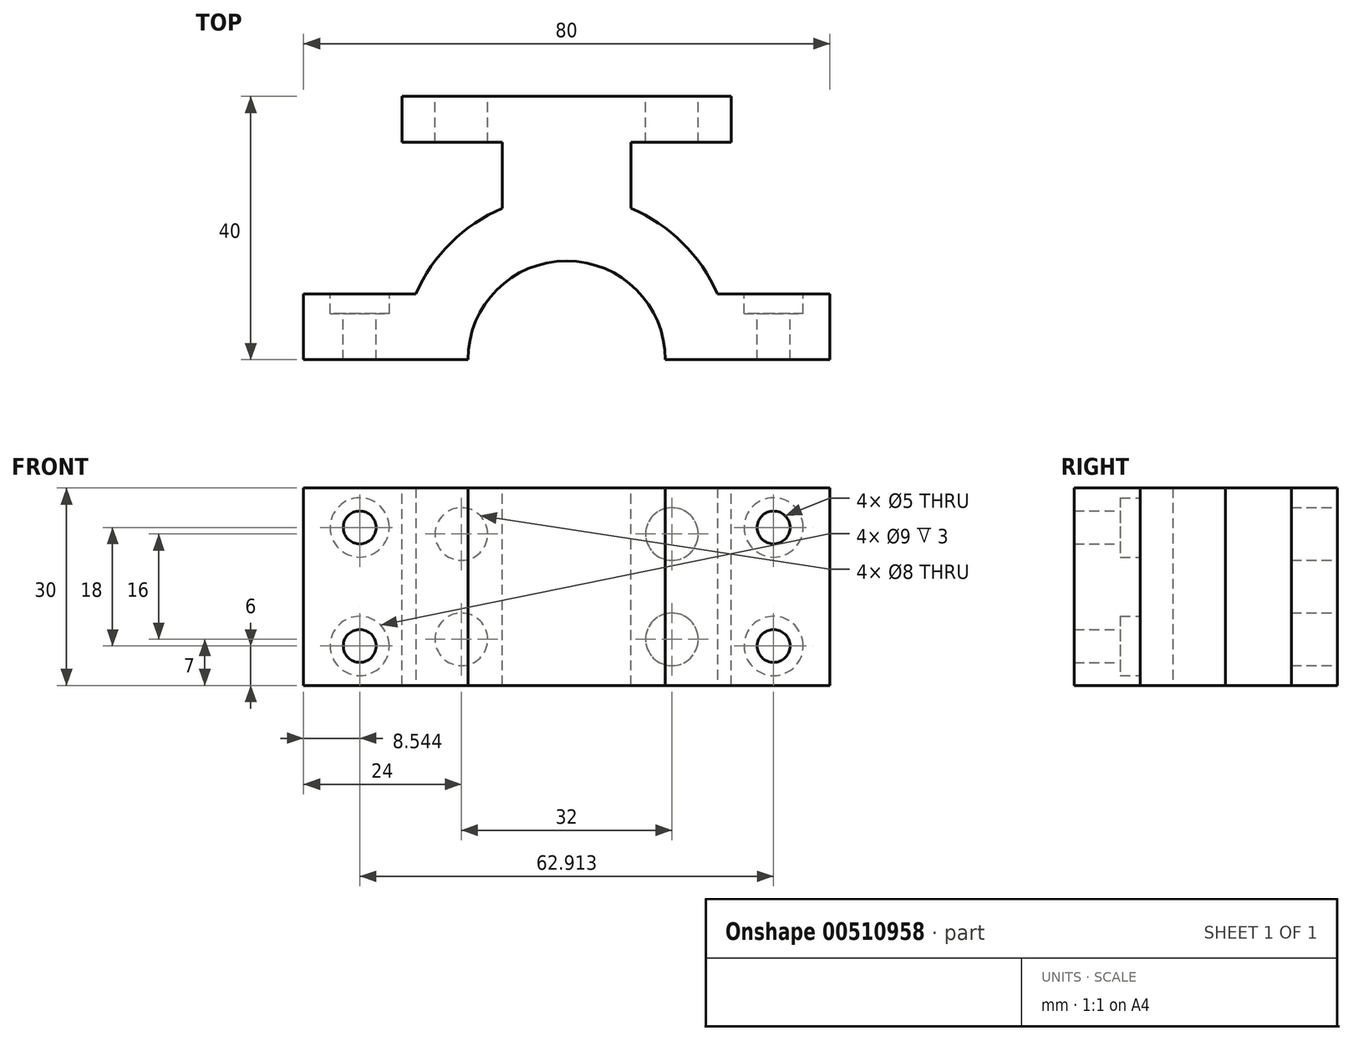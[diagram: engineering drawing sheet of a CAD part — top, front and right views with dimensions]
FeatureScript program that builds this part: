
annotation { "Feature Type Name" : "Feature", "Feature Type Description" : "" }
export const myFeature = defineFeature(function(context is Context, id is Id, definition is map)
    precondition{}
    {
        {
            var Q0;
            Q0=qCreatedBy(makeId("Top.planeOp"),FACE);
            var sketch = newSketch(context, id + "F0", { "sketchPlane" : qUnion([Q0])});
            skArc(sketch, "E0", {"start": v(15, 0) * mm, "mid": v(0, 15) * mm, "end": v(-15, 0) * mm});
            skArc(sketch, "E1.0", {"start": v(22.91, 10) * mm, "mid": v(0, 25) * mm, "end": v(-22.91, 10) * mm});
            skLineSegment(sketch, "E2", {"start": v(-22.91, 10) * mm, "end": v(-40, 10) * mm});
            skLineSegment(sketch, "E3", {"start": v(-40, 10) * mm, "end": v(-40, 0) * mm});
            skLineSegment(sketch, "E4", {"start": v(40, 0) * mm, "end": v(40, 10) * mm});
            skLineSegment(sketch, "E5", {"start": v(40, 10) * mm, "end": v(22.91, 10) * mm});
            skLineSegment(sketch, "E6", {"start": v(-40, 0) * mm, "end": v(-15, 0) * mm});
            skLineSegment(sketch, "E7", {"start": v(15, 0) * mm, "end": v(40, 0) * mm});
            skSolve(sketch);
        }
        {
            var Q0;
            Q0=qSketchRegion(id+"F0",true);
            extrude(context, id + "F1", {"entities" : qUnion([Q0]), "endBound" : BoundingType.SYMMETRIC, "depth" : 30 * mm});
        }
        {
            var Q0;
            Q0=makeQuery(id+"F1.opExtrude","SWEPT_FACE",FACE,{"disambiguationData":[OSD([sQuery(id+"F0.wireOp",EDGE,"E5")])]});
            var sketch = newSketch(context, id + "F2", { "sketchPlane" : qUnion([Q0])});
            skCircle(sketch, "E8", {"center": v(-31.46, 9) * mm, "radius": 2.5 * mm});
            skPoint(sketch, "E8.centerSnap0", {"position": v(-31.46, 15) * mm});
            skCircle(sketch, "E9.MirrorC", {"center": v(-31.46, -9) * mm, "radius": 2.5 * mm});
            skCircle(sketch, "E10.MirrorC", {"center": v(31.46, -9) * mm, "radius": 2.5 * mm});
            skCircle(sketch, "E11.MirrorC", {"center": v(31.46, 9) * mm, "radius": 2.5 * mm});
            skSolve(sketch);
        }
        {
            var Q0;
            Q0=qSketchRegion(id+"F2",true);
            extrude(context, id + "F3", {"entities" : qUnion([Q0]), "operationType" : NewBodyOperationType.REMOVE, "oppositeDirection" : true, "depth" : 15 * mm});
        }
        {
            var Q0;
            Q0=makeQuery(id+"F1.opExtrude","SWEPT_FACE",FACE,{"disambiguationData":[OSD([sQuery(id+"F0.wireOp",EDGE,"E2")])]});
            var sketch = newSketch(context, id + "F4", { "sketchPlane" : qUnion([Q0])});
            skCircle(sketch, "E12.0", {"center": v(31.46, 9) * mm, "radius": 2.5 * mm});
            skCircle(sketch, "E13.0", {"center": v(31.46, 9) * mm, "radius": 4.5 * mm});
            skCircle(sketch, "E14.MirrorC", {"center": v(31.46, -9) * mm, "radius": 4.5 * mm});
            skCircle(sketch, "E15.MirrorC", {"center": v(-31.46, -9) * mm, "radius": 4.5 * mm});
            skCircle(sketch, "E16.MirrorC", {"center": v(-31.46, 9) * mm, "radius": 4.5 * mm});
            skSolve(sketch);
        }
        {
            var Q0;
            Q0 = qSketchRegion(id + "F4", true);
            extrude(context, id + "F5", {"entities" : qUnion([Q0]), "operationType" : NewBodyOperationType.REMOVE, "oppositeDirection" : true, "depth" : 3 * mm});
        }
        {
            var Q0;
            Q0=makeQuery(id+"F1.opExtrude","CAP_FACE",FACE,{"disambiguationData":[OSD([sQuery(id+"F0.wireOp",EDGE,"E0"),sQuery(id+"F0.wireOp",EDGE,"E1.0"),sQuery(id+"F0.wireOp",EDGE,"E2"),sQuery(id+"F0.wireOp",EDGE,"E3"),sQuery(id+"F0.wireOp",EDGE,"E4"),sQuery(id+"F0.wireOp",EDGE,"E5"),sQuery(id+"F0.wireOp",EDGE,"E6"),sQuery(id+"F0.wireOp",EDGE,"E7")])],"isStart":false});
            var sketch = newSketch(context, id + "F6", { "sketchPlane" : qUnion([Q0])});
            skLineSegment(sketch, "E17.bottom", {"start": v(-9.8, 23) * mm, "end": v(9.8, 23) * mm});
            skLineSegment(sketch, "E17.top", {"start": v(-9.8, 33) * mm, "end": v(9.8, 33) * mm});
            skLineSegment(sketch, "E17.left", {"start": v(-9.8, 23) * mm, "end": v(-9.8, 33) * mm});
            skLineSegment(sketch, "E17.right", {"start": v(9.8, 23) * mm, "end": v(9.8, 33) * mm});
            skLineSegment(sketch, "E18.bottom", {"start": v(0, 33) * mm, "end": v(25, 33) * mm});
            skLineSegment(sketch, "E18.top", {"start": v(0, 40) * mm, "end": v(25, 40) * mm});
            skLineSegment(sketch, "E18.left", {"start": v(0, 33) * mm, "end": v(0, 40) * mm});
            skLineSegment(sketch, "E18.right", {"start": v(25, 33) * mm, "end": v(25, 40) * mm});
            skLineSegment(sketch, "E19.MirrorCS", {"start": v(0, 40) * mm, "end": v(-25, 40) * mm});
            skLineSegment(sketch, "E20.MirrorCS", {"start": v(-25, 33) * mm, "end": v(-25, 40) * mm});
            skLineSegment(sketch, "E21.MirrorCS", {"start": v(0, 33) * mm, "end": v(-25, 33) * mm});
            skSolve(sketch);
        }
        {
            var Q0;
            Q0 = qSketchRegion(id + "F6", true);
            extrude(context, id + "F7", {"entities" : qUnion([Q0]), "operationType" : NewBodyOperationType.ADD, "oppositeDirection" : true, "depth" : 30 * mm});
        }
        {
            var Q0;
            Q0=makeQuery(id+"F7.opExtrude","SWEPT_FACE",FACE,{"disambiguationData":[OSD([sQuery(id+"F6.wireOp",EDGE,"E18.top"),sQuery(id+"F6.wireOp",EDGE,"E19.MirrorCS")])]});
            var sketch = newSketch(context, id + "F8", { "sketchPlane" : qUnion([Q0])});
            skCircle(sketch, "E22", {"center": v(16, 8) * mm, "radius": 4 * mm});
            skCircle(sketch, "E23.MirrorC", {"center": v(16, -8) * mm, "radius": 4 * mm});
            skCircle(sketch, "E24.MirrorC", {"center": v(-16, -8) * mm, "radius": 4 * mm});
            skCircle(sketch, "E25.MirrorC", {"center": v(-16, 8) * mm, "radius": 4 * mm});
            skSolve(sketch);
        }
        {
            var Q0;
            Q0 = qSketchRegion(id + "F8", true);
            extrude(context, id + "F9", {"entities" : qUnion([Q0]), "operationType" : NewBodyOperationType.REMOVE, "oppositeDirection" : true, "depth" : 8 * mm});
        }
    });
